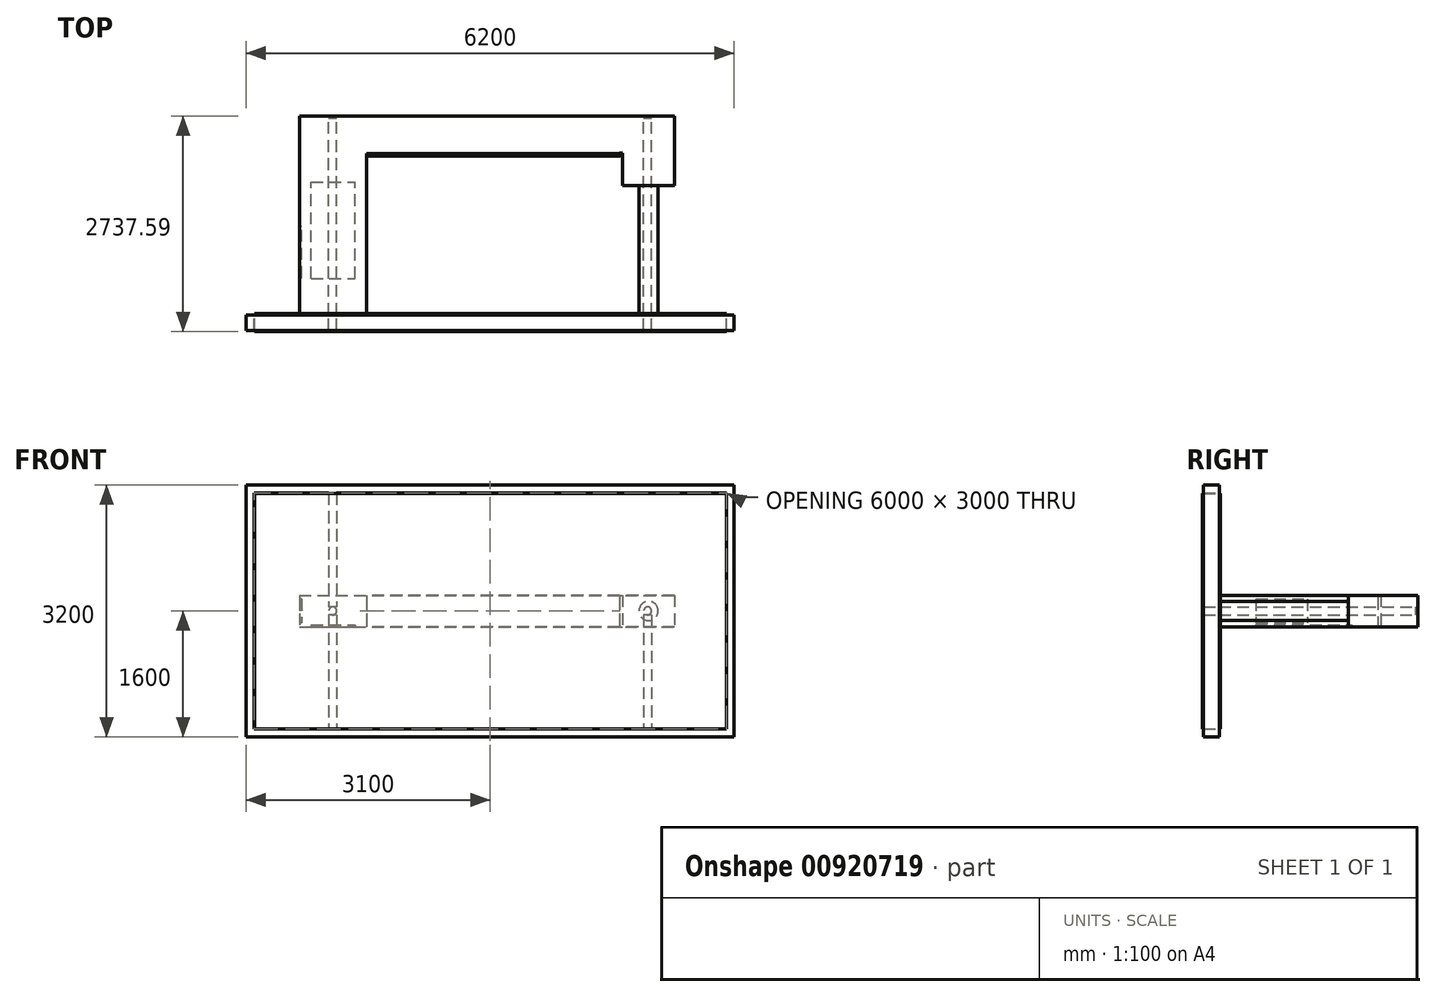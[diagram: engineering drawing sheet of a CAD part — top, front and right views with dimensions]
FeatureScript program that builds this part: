
annotation { "Feature Type Name" : "Feature", "Feature Type Description" : "" }
export const myFeature = defineFeature(function(context is Context, id is Id, definition is map)
    precondition{}
    {
        {
            var Q0;
            Q0=qCreatedBy(makeId("Front.planeOp"),FACE);
            var sketch = newSketch(context, id + "F0", { "sketchPlane" : qUnion([Q0])});
            skLineSegment(sketch, "E0", {"start": v(2000, 0) * mm, "end": v(-2000, 0) * mm});
            skCircle(sketch, "E1", {"center": v(2000, 0) * mm, "radius": 50 * mm});
            skCircle(sketch, "E2", {"center": v(-2000, 0) * mm, "radius": 50 * mm});
            skSolve(sketch);
        }
        {
            var Q0;
            Q0 = qSketchRegion(id + "F0", true);
            extrude(context, id + "F1", {"entities" : qUnion([Q0]), "endBound" : BoundingType.SYMMETRIC, "depth" : 2500 * mm, "offsetDistance" : 25 * mm});
        }
        {
            var Q0;
            Q0=makeQuery(id+"F1.opExtrude","CAP_FACE",FACE,{"disambiguationData":[OSD([sQuery(id+"F0.wireOp",EDGE,"E1")])],"isStart":false});
            var sketch = newSketch(context, id + "F2", { "sketchPlane" : qUnion([Q0])});
            skLineSegment(sketch, "E3.bottom", {"start": v(3000, 50) * mm, "end": v(-3000, 50) * mm});
            skLineSegment(sketch, "E3.top", {"start": v(3000, -50) * mm, "end": v(-3000, -50) * mm});
            skLineSegment(sketch, "E3.left", {"start": v(3000, 50) * mm, "end": v(3000, -50) * mm});
            skLineSegment(sketch, "E3.right", {"start": v(-3000, 50) * mm, "end": v(-3000, -50) * mm});
            skPoint(sketch, "E4.endSnap0", {"position": v(-3000, 0) * mm});
            skLineSegment(sketch, "E5", {"start": v(0, 50) * mm, "end": v(0, -50) * mm});
            skPoint(sketch, "E6.orphan", {"position": v(0, 309.34) * mm});
            skPoint(sketch, "E7.orphan", {"position": v(931.06, 0) * mm});
            skPoint(sketch, "E4.end.orphan", {"position": v(-940.56, 0) * mm});
            skLineSegment(sketch, "E8", {"start": v(2000, 0) * mm, "end": v(2000, 50) * mm});
            skPoint(sketch, "E9.firstSnap0", {"position": v(2000, 1500) * mm});
            skLineSegment(sketch, "E9.bottom", {"start": v(1950, 1500) * mm, "end": v(2050, 1500) * mm});
            skLineSegment(sketch, "E9.top", {"start": v(1950, -1500) * mm, "end": v(2050, -1500) * mm});
            skLineSegment(sketch, "E9.left", {"start": v(1950, 1500) * mm, "end": v(1950, -1500) * mm});
            skLineSegment(sketch, "E9.right", {"start": v(2050, 1500) * mm, "end": v(2050, -1500) * mm});
            skLineSegment(sketch, "E10", {"start": v(2000, 0) * mm, "end": v(1950, 0) * mm});
            skLineSegment(sketch, "E11.bottom", {"start": v(-2050, 1500) * mm, "end": v(-1950, 1500) * mm});
            skLineSegment(sketch, "E11.top", {"start": v(-2050, -1500) * mm, "end": v(-1950, -1500) * mm});
            skLineSegment(sketch, "E11.left", {"start": v(-2050, 1500) * mm, "end": v(-2050, -1500) * mm});
            skLineSegment(sketch, "E11.right", {"start": v(-1950, 1500) * mm, "end": v(-1950, -1500) * mm});
            skLineSegment(sketch, "E12.bottom", {"start": v(3000, -1500) * mm, "end": v(-3000, -1500) * mm});
            skLineSegment(sketch, "E12.top", {"start": v(3000, 1500) * mm, "end": v(-3000, 1500) * mm});
            skLineSegment(sketch, "E12.left", {"start": v(3000, -1500) * mm, "end": v(3000, 1500) * mm});
            skLineSegment(sketch, "E12.right", {"start": v(-3000, -1500) * mm, "end": v(-3000, 1500) * mm});
            skPoint(sketch, "E12.middle", {"position": v(0, 0) * mm});
            skLineSegment(sketch, "E13.bottom", {"start": v(50, -1500) * mm, "end": v(-50, -1500) * mm});
            skLineSegment(sketch, "E13.top", {"start": v(50, 1500) * mm, "end": v(-50, 1500) * mm});
            skLineSegment(sketch, "E13.left", {"start": v(50, -1500) * mm, "end": v(50, 1500) * mm});
            skLineSegment(sketch, "E13.right", {"start": v(-50, -1500) * mm, "end": v(-50, 1500) * mm});
            skLineSegment(sketch, "E14.bottom", {"start": v(3100, -1600) * mm, "end": v(-3100, -1600) * mm});
            skLineSegment(sketch, "E14.top", {"start": v(3100, 1600) * mm, "end": v(-3100, 1600) * mm});
            skLineSegment(sketch, "E14.left", {"start": v(3100, -1600) * mm, "end": v(3100, 1600) * mm});
            skLineSegment(sketch, "E14.right", {"start": v(-3100, -1600) * mm, "end": v(-3100, 1600) * mm});
            skLineSegment(sketch, "E15.trimOffspring", {"start": v(50, 0) * mm, "end": v(-50, 0) * mm});
            skLineSegment(sketch, "E16.trimOffspring", {"start": v(2000, 1500) * mm, "end": v(2000, 3000) * mm});
            skSolve(sketch);
        }
        {
            var Q0;
            Q0 = qSketchRegion(id + "F2", true);
            var Q1;
            {var subQ1=sQuery(id+"F2.wireOp",EDGE,"E9.right");var subQ3=sQuery(id+"F2.wireOp",EDGE,"E3.top");var subQ4=makeQuery(id+"F2.imprint","INTERSECT",VERTEX,{"derivedFrom":[subQ3,subQ1]});Q1=makeQuery(id+"F2.imprint","IMPRINT",FACE,{"disambiguationData":[TD([[makeQuery(id+"F2.imprint","IMPRINT",EDGE,{"disambiguationData":[TD([[subQ4,-1.0]])],"derivedFrom":subQ3}),1.0]])]});}
            var Q2;
            {var subQ0=sQuery(id+"F2.wireOp",EDGE,"E12.top");var subQ9=makeQuery(id+"F2.imprint","IMPRINT",VERTEX,{"derivedFrom":subQ0});Q2=makeQuery(id+"F2.imprint","IMPRINT",FACE,{"disambiguationData":[TD([[makeQuery(id+"F2.imprint","IMPRINT",EDGE,{"disambiguationData":[TD([[subQ9,1.0]])],"derivedFrom":subQ0}),1.0]])]});}
            var Q3;
            {var subQ1=sQuery(id+"F2.wireOp",EDGE,"E13.bottom");Q3=makeQuery(id+"F2.imprint","IMPRINT",FACE,{"disambiguationData":[TD([[makeQuery(id+"F2.imprint","IMPRINT",EDGE,{"derivedFrom":subQ1}),-1.0]])]});}
            var Q4;
            {var subQ0=sQuery(id+"F2.wireOp",EDGE,"E13.top");Q4=makeQuery(id+"F2.imprint","IMPRINT",FACE,{"disambiguationData":[TD([[makeQuery(id+"F2.imprint","IMPRINT",EDGE,{"derivedFrom":subQ0}),1.0]])]});}
            var Q5;
            {var subQ0=sQuery(id+"F2.wireOp",EDGE,"E11.right");var subQ1=sQuery(id+"F2.wireOp",EDGE,"E3.bottom");var subQ2=makeQuery(id+"F2.imprint","INTERSECT",VERTEX,{"derivedFrom":[subQ1,subQ0]});Q5=makeQuery(id+"F2.imprint","IMPRINT",FACE,{"disambiguationData":[TD([[makeQuery(id+"F2.imprint","IMPRINT",EDGE,{"disambiguationData":[TD([[subQ2,-1.0]])],"derivedFrom":subQ1}),-1.0]])]});}
            var Q6;
            {var subQ0=sQuery(id+"F2.wireOp",EDGE,"E11.right");var subQ1=sQuery(id+"F2.wireOp",EDGE,"E3.top");var subQ2=makeQuery(id+"F2.imprint","INTERSECT",VERTEX,{"derivedFrom":[subQ1,subQ0]});Q6=makeQuery(id+"F2.imprint","IMPRINT",FACE,{"disambiguationData":[TD([[makeQuery(id+"F2.imprint","IMPRINT",EDGE,{"disambiguationData":[TD([[subQ2,-1.0]])],"derivedFrom":subQ1}),1.0]])]});}
            extrude(context, id + "F3", {"entities" : qUnion([Q0, Q1, Q2, Q3, Q4, Q5, Q6]), "depth" : 200 * mm, "offsetDistance" : 25 * mm});
        }
        {
            var Q0;
            Q0=qCreatedBy(makeId("Top.planeOp"),FACE);
            var sketch = newSketch(context, id + "F4", { "sketchPlane" : qUnion([Q0])});
            skLineSegment(sketch, "E17.bottom", {"start": v(-2421.68, -1233.25) * mm, "end": v(-1569.93, -1233.25) * mm});
            skLineSegment(sketch, "E17.top", {"start": v(-2421.68, 1275.3) * mm, "end": v(-1569.93, 1275.3) * mm});
            skLineSegment(sketch, "E17.left", {"start": v(-2421.68, -1233.25) * mm, "end": v(-2421.68, 1275.3) * mm});
            skLineSegment(sketch, "E17.right", {"start": v(-1569.93, -1233.25) * mm, "end": v(-1569.93, 1275.3) * mm});
            skLineSegment(sketch, "E18.bottom", {"start": v(-1569.93, 1275.3) * mm, "end": v(2344.58, 1275.3) * mm});
            skLineSegment(sketch, "E18.top", {"start": v(-1569.93, 802.76) * mm, "end": v(2344.58, 802.76) * mm});
            skLineSegment(sketch, "E18.left", {"start": v(-1569.93, 1275.3) * mm, "end": v(-1569.93, 802.76) * mm});
            skLineSegment(sketch, "E18.right", {"start": v(2344.58, 1275.3) * mm, "end": v(2344.58, 802.76) * mm});
            skLineSegment(sketch, "E19.bottom", {"start": v(2344.58, 802.76) * mm, "end": v(1679.52, 802.76) * mm});
            skLineSegment(sketch, "E19.top", {"start": v(2344.58, 388.56) * mm, "end": v(1679.52, 388.56) * mm});
            skLineSegment(sketch, "E19.left", {"start": v(2344.58, 802.76) * mm, "end": v(2344.58, 388.56) * mm});
            skLineSegment(sketch, "E19.right", {"start": v(1679.52, 802.76) * mm, "end": v(1679.52, 388.56) * mm});
            skSolve(sketch);
        }
        {
            var Q0;
            {var subQ8=sQuery(id+"F4.wireOp",EDGE,"E18.bottom");var subQ11=sQuery(id+"F4.wireOp",EDGE,"E17.bottom");Q0=qUnion([makeQuery(id+"F4.imprint","IMPRINT",FACE,{"disambiguationData":[TD([[makeQuery(id+"F4.imprint","IMPRINT",EDGE,{"derivedFrom":subQ11}),1.0]])]}),makeQuery(id+"F4.imprint","IMPRINT",FACE,{"disambiguationData":[TD([[makeQuery(id+"F4.imprint","IMPRINT",EDGE,{"derivedFrom":sQuery(id+"F4.wireOp",EDGE,"E19.top")}),-1.0]])]}),makeQuery(id+"F4.imprint","IMPRINT",FACE,{"disambiguationData":[TD([[makeQuery(id+"F4.imprint","IMPRINT",EDGE,{"derivedFrom":subQ8}),-1.0]])]})]);}
            extrude(context, id + "F5", {"entities" : qUnion([Q0]), "endBound" : BoundingType.SYMMETRIC, "depth" : 400 * mm, "offsetDistance" : 25 * mm});
        }
        {
            var Q0;
            Q0=makeQuery(id+"F5.opExtrude","CAP_FACE",FACE,{"disambiguationData":[OSD([sQuery(id+"F4.wireOp",EDGE,"E17.bottom"),sQuery(id+"F4.wireOp",EDGE,"E17.top"),sQuery(id+"F4.wireOp",EDGE,"E17.left"),sQuery(id+"F4.wireOp",EDGE,"E17.right"),sQuery(id+"F4.wireOp",EDGE,"E18.bottom"),sQuery(id+"F4.wireOp",EDGE,"E18.top"),sQuery(id+"F4.wireOp",EDGE,"E18.right"),sQuery(id+"F4.wireOp",EDGE,"E19.top"),sQuery(id+"F4.wireOp",EDGE,"E19.left"),sQuery(id+"F4.wireOp",EDGE,"E19.right")])],"isStart":true});
            var sketch = newSketch(context, id + "F6", { "sketchPlane" : qUnion([Q0])});
            skLineSegment(sketch, "E20.bottom", {"start": v(-2273.29, 788.18) * mm, "end": v(-1714.07, 788.18) * mm});
            skLineSegment(sketch, "E20.top", {"start": v(-2273.29, -436.4) * mm, "end": v(-1714.07, -436.4) * mm});
            skLineSegment(sketch, "E20.left", {"start": v(-2273.29, 788.18) * mm, "end": v(-2273.29, -436.4) * mm});
            skLineSegment(sketch, "E20.right", {"start": v(-1714.07, 788.18) * mm, "end": v(-1714.07, -436.4) * mm});
            skSolve(sketch);
        }
        {
            var Q0;
            Q0 = qSketchRegion(id + "F6", true);
            extrude(context, id + "F7", {"entities" : qUnion([Q0]), "operationType" : NewBodyOperationType.REMOVE, "oppositeDirection" : true, "depth" : 25 * mm, "offsetDistance" : 25 * mm});
        }
        {
            var Q0;
            Q0=makeQuery(id+"F5.opExtrude","SWEPT_FACE",FACE,{"disambiguationData":[OSD([sQuery(id+"F4.wireOp",EDGE,"E17.left")])]});
            var sketch = newSketch(context, id + "F8", { "sketchPlane" : qUnion([Q0])});
            skLineSegment(sketch, "E21.bottom", {"start": v(781, 151.73) * mm, "end": v(127.16, 151.73) * mm});
            skLineSegment(sketch, "E21.top", {"start": v(781, -154.1) * mm, "end": v(127.16, -154.1) * mm});
            skLineSegment(sketch, "E21.left", {"start": v(781, 151.73) * mm, "end": v(781, -154.1) * mm});
            skLineSegment(sketch, "E21.right", {"start": v(127.16, 151.73) * mm, "end": v(127.16, -154.1) * mm});
            skSolve(sketch);
        }
        {
            var Q0;
            Q0 = qSketchRegion(id + "F8", true);
            extrude(context, id + "F9", {"entities" : qUnion([Q0]), "operationType" : NewBodyOperationType.REMOVE, "oppositeDirection" : true, "depth" : 25 * mm, "offsetDistance" : 25 * mm});
        }
        {
            var Q0;
            Q0=makeQuery(id+"F5.opExtrude","SWEPT_FACE",FACE,{"disambiguationData":[OSD([sQuery(id+"F4.wireOp",EDGE,"E19.top")])]});
            var sketch = newSketch(context, id + "F10", { "sketchPlane" : qUnion([Q0])});
            skCircle(sketch, "E22", {"center": v(2012.05, 0) * mm, "radius": 121.28 * mm});
            skPoint(sketch, "E22.centerSnap0", {"position": v(2012.05, 200) * mm});
            skSolve(sketch);
        }
        {
            var Q0;
            Q0 = qSketchRegion(id + "F10", true);
            extrude(context, id + "F11", {"entities" : qUnion([Q0]), "depth" : 1640.9 * mm, "offsetDistance" : 25 * mm});
        }
        {
            var Q0;
            Q0=makeQuery(id+"F5.opExtrude","SWEPT_FACE",FACE,{"disambiguationData":[OSD([sQuery(id+"F4.wireOp",EDGE,"E17.bottom")])]});
            var sketch = newSketch(context, id + "F12", { "sketchPlane" : qUnion([Q0])});
            skLineSegment(sketch, "E23.bottom", {"start": v(-2992.8, 1493.46) * mm, "end": v(3004.56, 1493.46) * mm});
            skLineSegment(sketch, "E23.top", {"start": v(-2992.8, -1499.34) * mm, "end": v(3004.56, -1499.34) * mm});
            skLineSegment(sketch, "E23.left", {"start": v(-2992.8, 1493.46) * mm, "end": v(-2992.8, -1499.34) * mm});
            skLineSegment(sketch, "E23.right", {"start": v(3004.56, 1493.46) * mm, "end": v(3004.56, -1499.34) * mm});
            skSolve(sketch);
        }
        {
            var Q0;
            Q0 = qSketchRegion(id + "F12", true);
            extrude(context, id + "F13", {"entities" : qUnion([Q0]), "depth" : 229.03 * mm, "offsetDistance" : 25 * mm});
        }
        {
            var Q0;
            Q0=makeQuery(id+"F5.opExtrude","SWEPT_FACE",FACE,{"disambiguationData":[OSD([sQuery(id+"F4.wireOp",EDGE,"E17.right")])]});
            var sketch = newSketch(context, id + "F14", { "sketchPlane" : qUnion([Q0])});
            skLineSegment(sketch, "E24", {"start": v(763.98, 162.27) * mm, "end": v(763.98, -165.05) * mm});
            skArc(sketch, "E25", {"start": v(763.98, 162.27) * mm, "mid": v(775.4, 189.32) * mm, "end": v(802.76, 200) * mm});
            skArc(sketch, "E26", {"start": v(763.98, -165.05) * mm, "mid": v(775.6, -191.15) * mm, "end": v(802.76, -200) * mm});
            skLineSegment(sketch, "E27", {"start": v(802.76, 200) * mm, "end": v(802.76, -200) * mm});
            skSolve(sketch);
        }
        {
            var Q0;
            {var subQ1=sQuery(id+"F14.wireOp",EDGE,"E24");Q0=makeQuery(id+"F14.imprint","IMPRINT",FACE,{"disambiguationData":[TD([[makeQuery(id+"F14.imprint","IMPRINT",EDGE,{"derivedFrom":subQ1}),1.0]])]});}
            extrude(context, id + "F15", {"entities" : qUnion([Q0]), "operationType" : NewBodyOperationType.ADD, "depth" : 3214.08 * mm, "offsetDistance" : 25 * mm});
        }
    });
